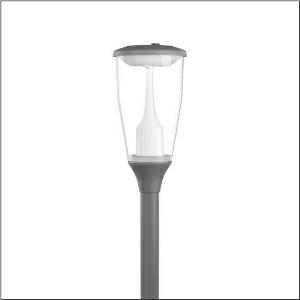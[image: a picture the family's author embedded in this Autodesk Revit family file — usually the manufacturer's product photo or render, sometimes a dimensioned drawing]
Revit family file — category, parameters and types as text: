
# Revit family: dl_11_iq___st1_2a_5xa5565ev14h000022_6439
name_source: partatom
category: Lighting Fixtures
units: mm (PartAtom-declared; Revit-internal decimal feet)

## family parameters
Cut with Voids When Loaded = No
Host = Face
Light Source = No
Part Type = Normal
Room Calculation Point = No
Round Connector Dimension = Use Diameter
Shared = No

## types (1)
- --- (1 x LED, 1560 lm, 10.7 W, 3000K)
    Apparent Load = 11 VA
    CIE Flux Codes = 24 63 94 96 100
    Color Rendering = 70
    Color Temperature = 3000K
    Default Elevation = 1800 mm
    Description = DL 11 iQ, mast luminaire, Module 540 iQ-SR, primary light control with 3 zone facetted reflector, of plastic, silver coated, highly specular, structured, primary optical cover: cover, of PMMA, transparent, light distribution: ST1.2a, light emission: direct distribution, primary light characteristic: asymmetric, installation type: post-top, LED, High Power LED, rated luminous flux: 1.560lm, luminous efficacy: 146lm/W, light colour: 730, colour temperature: 3000K, control gear: iQ-Street Remote, D4i with power reduction, control: pre-setting: logarithmic dimming characteristic, Street-Remote, Auto-Match, Temp-Guard, Lumen-Switch, Night-Set, Smart-Wire, Light-Fading, Desk-Remote (wireless, voltage-free reading and setting of iQ features in the workshop via application-optimized NFC function/RFID function), optimised constant luminous flux control (CLO 2.0), mains connection: 220..240V, AC, 50/60Hz, connection cable pre-assembled, cable length: 5,5m, start of lifetime: 11W, end of service life: 11W, reduction: 6W, luminaire housing, upper part, of diecast aluminium, coated, Siteco® metallic grey (DB 702S), spigot size: 60mm (post-top), mounting height: 3..5m, post-top mast mounting element, of diecast aluminium, coated, Siteco® metallic grey (DB 702S), Module 540 iQ-SR, traffic white (RAL 9016), equipment: standard, Smart Interface above, protection rating (complete): IP66, insulation class (complete): insulation class II (safety insulation), certification: CE, ENEC, ENEC+, VDE, impact resistance: IK07, packaging unit: 1 piece

Light Distribution: ST1.2a
    Height = 665 mm
    Lamp = 1 x LED
    Lamp Light Flux = 1560 lm
    Lamp Power = 10.7 W
    Lamp count = 1
    Length = 334 mm
    Luminous efficacy = 146 lm/W
    Manufacturer = Siteco
    ModVariant = No
    Model = 5XA5565EV14H000022
    Number of Poles = 1
    OnlyDefault = Yes
    Power Factor = 1
    Product Name = DL 11 iQ | ST1.2a
    Product group = mast luminaire | pylon top
    ProductGroupID = 6100
    Protection Class = Protection class II
    Protection Degree = IP 66
    RLX_Detail_Level = 1
    RLX_Emergency_Light_Flux = 0 lm
    RLX_Emergency_Type = 0
    RLX_Emergency_Type_DB = No
    RlxData = <blob elided: 140729 chars, md5=e3919790>
    Socket = socket
    Standby Power = 0 W
    System Light Flux = 1560 lm
    System Power = 11 W
    Type Comments = factory setting: luminous flux: 100 % | dim-lin: 254 | 419 mA
    Type Image = l_1337541.jpg
    URL = http://relux.com
    VarID = @adj_116627
    Voltage = 0 V
    Weight = 0.00 kg
    Width = 0 mm  [stored 0 ft]

note: [stored X ft] marks values corroborated as IEEE doubles in the binary element streams (Revit-internal decimal feet)

## geometry (parser evidence)
native form markers: Blend x4, Sweep x10
no freeform markers — native parametric forms only
